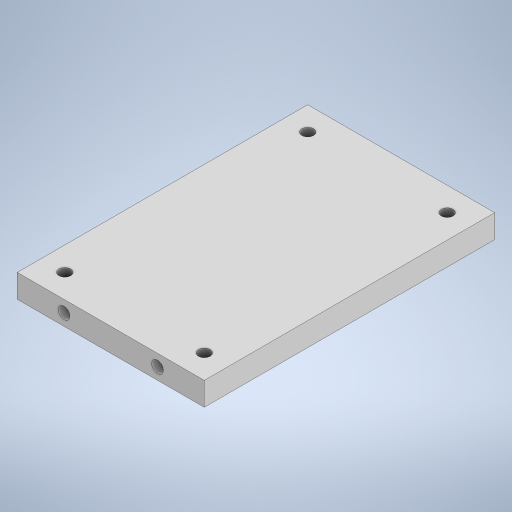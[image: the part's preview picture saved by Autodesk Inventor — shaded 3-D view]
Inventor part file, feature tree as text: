
AUTODESK INVENTOR PART (.ipt)
format: ipt  version: 2024 (Build 280153000, 153)  size: 286,720 bytes
history: native  units: in
note: dims shown in document units (in); Inventor stores cm internally (conversion verified against a paired STEP export)
features: extrude x4, sketch x4
ambient origin geometry x8: Origin, YZ Plane, XZ Plane, XY Plane, X Axis, Y Axis, Z Axis, Center Point
bodies: Solid1 (feature_tree)
feature tree (8):
  extrude  "Extrusion1"  Depth=12.228in
  extrude  "Extrusion2"  Depth=0.984in
  sketch  "Sketch3"  dims[d5=1.0in d6=1.0in]
  sketch  "Sketch4"  dims[d7=0.5in d8=1.0in d9=1.0in d10=1.0in d11=1.0in d12=0.5in d13=0.5in d14=1.0in d15=1.0in d16=0.984in d17=0.0in d18=0.5in d19=1.9685in d20=0.492in d21=0.492in d22=1.9685in d23=0.5in d24=0.5in d25=0.5in d26=1.9685in d27=0.492in d28=0.492in d29=1.9685in d30=0.7874in d31=0.0in d32=0.7874in d33=0.0in]
  extrude  "Extrusion3"  Depth=1.0in
  extrude  "Extrusion4"  Depth=0.7874in
  sketch  "Sketch1"  dims[d0=7.874in d1=12.228in]
  sketch  "Sketch2"  dims[d2=0.984in d3=0.0in d4=0.5in]
